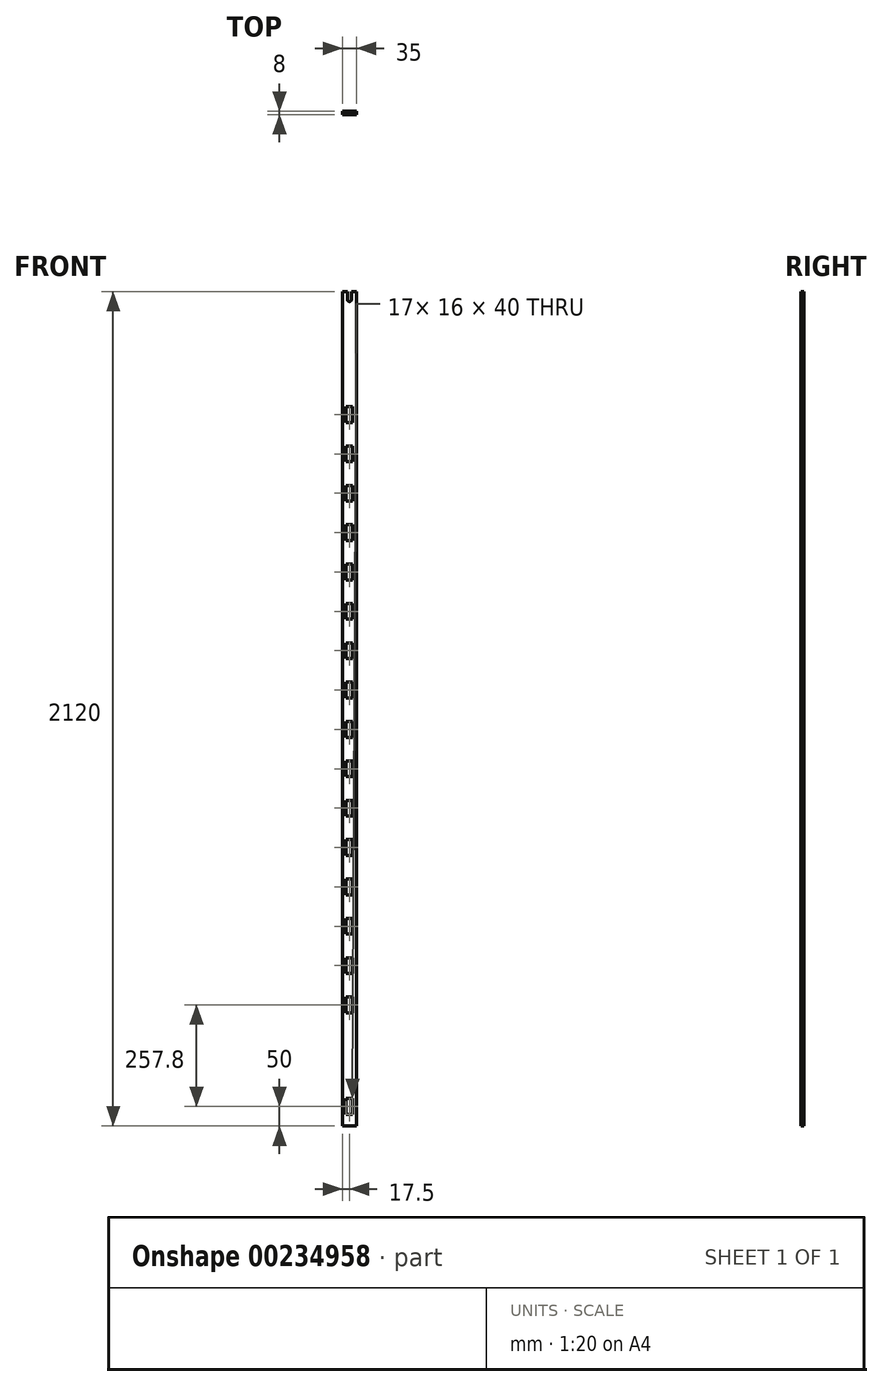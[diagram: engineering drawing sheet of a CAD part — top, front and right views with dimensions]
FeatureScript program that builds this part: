
annotation { "Feature Type Name" : "Feature", "Feature Type Description" : "" }
export const myFeature = defineFeature(function(context is Context, id is Id, definition is map)
    precondition{}
    {
        {
            var Q0;
            Q0=qCreatedBy(makeId("Front.planeOp"),FACE);
            var sketch = newSketch(context, id + "F0", { "sketchPlane" : qUnion([Q0])});
            skLineSegment(sketch, "E0.bottom", {"start": v(0, 0) * mm, "end": v(12.25, 0) * mm});
            skLineSegment(sketch, "E0.top", {"start": v(0, -2120) * mm, "end": v(35, -2120) * mm});
            skLineSegment(sketch, "E0.left", {"start": v(0, 0) * mm, "end": v(0, -2120) * mm});
            skLineSegment(sketch, "E0.right", {"start": v(35, 0) * mm, "end": v(35, -2120) * mm});
            skLineSegment(sketch, "E1.0", {"start": v(17.5, 0) * mm, "end": v(17.5, -2120) * mm, "construction": true});
            skLineSegment(sketch, "E2.left", {"start": v(12.25, 0) * mm, "end": v(12.25, -19.75) * mm});
            skLineSegment(sketch, "E2.right", {"start": v(22.75, 0) * mm, "end": v(22.75, -19.75) * mm});
            skLineSegment(sketch, "E3.bottom", {"start": v(9.5, -292.2) * mm, "end": v(25.5, -292.2) * mm});
            skLineSegment(sketch, "E3.top", {"start": v(9.5, -332.2) * mm, "end": v(25.5, -332.2) * mm});
            skLineSegment(sketch, "E3.left", {"start": v(9.5, -292.2) * mm, "end": v(9.5, -332.2) * mm});
            skLineSegment(sketch, "E3.right", {"start": v(25.5, -292.2) * mm, "end": v(25.5, -332.2) * mm});
            skArc(sketch, "E4", {"start": v(12.25, -19.75) * mm, "mid": v(17.5, -25) * mm, "end": v(22.75, -19.75) * mm});
            skLineSegment(sketch, "E5.0.1.0", {"start": v(9.5, -432.2) * mm, "end": v(25.5, -432.2) * mm});
            skLineSegment(sketch, "E5.0.1.1", {"start": v(25.5, -392.2) * mm, "end": v(25.5, -432.2) * mm});
            skLineSegment(sketch, "E5.0.1.2", {"start": v(9.5, -392.2) * mm, "end": v(25.5, -392.2) * mm});
            skLineSegment(sketch, "E5.0.1.3", {"start": v(9.5, -392.2) * mm, "end": v(9.5, -432.2) * mm});
            skLineSegment(sketch, "E5.0.2.0", {"start": v(9.5, -532.2) * mm, "end": v(25.5, -532.2) * mm});
            skLineSegment(sketch, "E5.0.2.1", {"start": v(25.5, -492.2) * mm, "end": v(25.5, -532.2) * mm});
            skLineSegment(sketch, "E5.0.2.2", {"start": v(9.5, -492.2) * mm, "end": v(25.5, -492.2) * mm});
            skLineSegment(sketch, "E5.0.2.3", {"start": v(9.5, -492.2) * mm, "end": v(9.5, -532.2) * mm});
            skLineSegment(sketch, "E5.0.3.0", {"start": v(9.5, -632.2) * mm, "end": v(25.5, -632.2) * mm});
            skLineSegment(sketch, "E5.0.3.1", {"start": v(25.5, -592.2) * mm, "end": v(25.5, -632.2) * mm});
            skLineSegment(sketch, "E5.0.3.2", {"start": v(9.5, -592.2) * mm, "end": v(25.5, -592.2) * mm});
            skLineSegment(sketch, "E5.0.3.3", {"start": v(9.5, -592.2) * mm, "end": v(9.5, -632.2) * mm});
            skLineSegment(sketch, "E5.0.4.0", {"start": v(9.5, -732.2) * mm, "end": v(25.5, -732.2) * mm});
            skLineSegment(sketch, "E5.0.4.1", {"start": v(25.5, -692.2) * mm, "end": v(25.5, -732.2) * mm});
            skLineSegment(sketch, "E5.0.4.2", {"start": v(9.5, -692.2) * mm, "end": v(25.5, -692.2) * mm});
            skLineSegment(sketch, "E5.0.4.3", {"start": v(9.5, -692.2) * mm, "end": v(9.5, -732.2) * mm});
            skLineSegment(sketch, "E5.0.5.0", {"start": v(9.5, -832.2) * mm, "end": v(25.5, -832.2) * mm});
            skLineSegment(sketch, "E5.0.5.1", {"start": v(25.5, -792.2) * mm, "end": v(25.5, -832.2) * mm});
            skLineSegment(sketch, "E5.0.5.2", {"start": v(9.5, -792.2) * mm, "end": v(25.5, -792.2) * mm});
            skLineSegment(sketch, "E5.0.5.3", {"start": v(9.5, -792.2) * mm, "end": v(9.5, -832.2) * mm});
            skLineSegment(sketch, "E5.0.6.0", {"start": v(9.5, -932.2) * mm, "end": v(25.5, -932.2) * mm});
            skLineSegment(sketch, "E5.0.6.1", {"start": v(25.5, -892.2) * mm, "end": v(25.5, -932.2) * mm});
            skLineSegment(sketch, "E5.0.6.2", {"start": v(9.5, -892.2) * mm, "end": v(25.5, -892.2) * mm});
            skLineSegment(sketch, "E5.0.6.3", {"start": v(9.5, -892.2) * mm, "end": v(9.5, -932.2) * mm});
            skLineSegment(sketch, "E5.0.7.0", {"start": v(9.5, -1032.2) * mm, "end": v(25.5, -1032.2) * mm});
            skLineSegment(sketch, "E5.0.7.1", {"start": v(25.5, -992.2) * mm, "end": v(25.5, -1032.2) * mm});
            skLineSegment(sketch, "E5.0.7.2", {"start": v(9.5, -992.2) * mm, "end": v(25.5, -992.2) * mm});
            skLineSegment(sketch, "E5.0.7.3", {"start": v(9.5, -992.2) * mm, "end": v(9.5, -1032.2) * mm});
            skLineSegment(sketch, "E5.0.8.0", {"start": v(9.5, -1132.2) * mm, "end": v(25.5, -1132.2) * mm});
            skLineSegment(sketch, "E5.0.8.1", {"start": v(25.5, -1092.2) * mm, "end": v(25.5, -1132.2) * mm});
            skLineSegment(sketch, "E5.0.8.2", {"start": v(9.5, -1092.2) * mm, "end": v(25.5, -1092.2) * mm});
            skLineSegment(sketch, "E5.0.8.3", {"start": v(9.5, -1092.2) * mm, "end": v(9.5, -1132.2) * mm});
            skLineSegment(sketch, "E5.0.9.0", {"start": v(9.5, -1232.2) * mm, "end": v(25.5, -1232.2) * mm});
            skLineSegment(sketch, "E5.0.9.1", {"start": v(25.5, -1192.2) * mm, "end": v(25.5, -1232.2) * mm});
            skLineSegment(sketch, "E5.0.9.2", {"start": v(9.5, -1192.2) * mm, "end": v(25.5, -1192.2) * mm});
            skLineSegment(sketch, "E5.0.9.3", {"start": v(9.5, -1192.2) * mm, "end": v(9.5, -1232.2) * mm});
            skLineSegment(sketch, "E5.0.10.0", {"start": v(9.5, -1332.2) * mm, "end": v(25.5, -1332.2) * mm});
            skLineSegment(sketch, "E5.0.10.1", {"start": v(25.5, -1292.2) * mm, "end": v(25.5, -1332.2) * mm});
            skLineSegment(sketch, "E5.0.10.2", {"start": v(9.5, -1292.2) * mm, "end": v(25.5, -1292.2) * mm});
            skLineSegment(sketch, "E5.0.10.3", {"start": v(9.5, -1292.2) * mm, "end": v(9.5, -1332.2) * mm});
            skLineSegment(sketch, "E5.0.11.0", {"start": v(9.5, -1432.2) * mm, "end": v(25.5, -1432.2) * mm});
            skLineSegment(sketch, "E5.0.11.1", {"start": v(25.5, -1392.2) * mm, "end": v(25.5, -1432.2) * mm});
            skLineSegment(sketch, "E5.0.11.2", {"start": v(9.5, -1392.2) * mm, "end": v(25.5, -1392.2) * mm});
            skLineSegment(sketch, "E5.0.11.3", {"start": v(9.5, -1392.2) * mm, "end": v(9.5, -1432.2) * mm});
            skLineSegment(sketch, "E5.0.12.0", {"start": v(9.5, -1532.2) * mm, "end": v(25.5, -1532.2) * mm});
            skLineSegment(sketch, "E5.0.12.1", {"start": v(25.5, -1492.2) * mm, "end": v(25.5, -1532.2) * mm});
            skLineSegment(sketch, "E5.0.12.2", {"start": v(9.5, -1492.2) * mm, "end": v(25.5, -1492.2) * mm});
            skLineSegment(sketch, "E5.0.12.3", {"start": v(9.5, -1492.2) * mm, "end": v(9.5, -1532.2) * mm});
            skLineSegment(sketch, "E5.0.13.0", {"start": v(9.5, -1632.2) * mm, "end": v(25.5, -1632.2) * mm});
            skLineSegment(sketch, "E5.0.13.1", {"start": v(25.5, -1592.2) * mm, "end": v(25.5, -1632.2) * mm});
            skLineSegment(sketch, "E5.0.13.2", {"start": v(9.5, -1592.2) * mm, "end": v(25.5, -1592.2) * mm});
            skLineSegment(sketch, "E5.0.13.3", {"start": v(9.5, -1592.2) * mm, "end": v(9.5, -1632.2) * mm});
            skLineSegment(sketch, "E5.0.14.0", {"start": v(9.5, -1732.2) * mm, "end": v(25.5, -1732.2) * mm});
            skLineSegment(sketch, "E5.0.14.1", {"start": v(25.5, -1692.2) * mm, "end": v(25.5, -1732.2) * mm});
            skLineSegment(sketch, "E5.0.14.2", {"start": v(9.5, -1692.2) * mm, "end": v(25.5, -1692.2) * mm});
            skLineSegment(sketch, "E5.0.14.3", {"start": v(9.5, -1692.2) * mm, "end": v(9.5, -1732.2) * mm});
            skLineSegment(sketch, "E5.0.15.0", {"start": v(9.5, -1832.2) * mm, "end": v(25.5, -1832.2) * mm});
            skLineSegment(sketch, "E5.0.15.1", {"start": v(25.5, -1792.2) * mm, "end": v(25.5, -1832.2) * mm});
            skLineSegment(sketch, "E5.0.15.2", {"start": v(9.5, -1792.2) * mm, "end": v(25.5, -1792.2) * mm});
            skLineSegment(sketch, "E5.0.15.3", {"start": v(9.5, -1792.2) * mm, "end": v(9.5, -1832.2) * mm});
            skLineSegment(sketch, "E5.direction1", {"start": v(9.5, -332.2) * mm, "end": v(34.5, -332.2) * mm, "construction": true});
            skLineSegment(sketch, "E5.direction2", {"start": v(9.5, -332.2) * mm, "end": v(9.5, -432.2) * mm, "construction": true});
            skLineSegment(sketch, "E6.bottom", {"start": v(25.5, -2050) * mm, "end": v(9.5, -2050) * mm});
            skLineSegment(sketch, "E6.top", {"start": v(25.5, -2090) * mm, "end": v(9.5, -2090) * mm});
            skLineSegment(sketch, "E6.left", {"start": v(25.5, -2050) * mm, "end": v(25.5, -2090) * mm});
            skLineSegment(sketch, "E6.right", {"start": v(9.5, -2050) * mm, "end": v(9.5, -2090) * mm});
            skLineSegment(sketch, "E7.trimOffspring", {"start": v(22.75, 0) * mm, "end": v(35, 0) * mm});
            skSolve(sketch);
        }
        {
            var Q0;
            Q0 = qSketchRegion(id + "F0", true);
            extrude(context, id + "F1", {"entities" : qUnion([Q0]), "depth" : 8 * mm});
        }
    });
